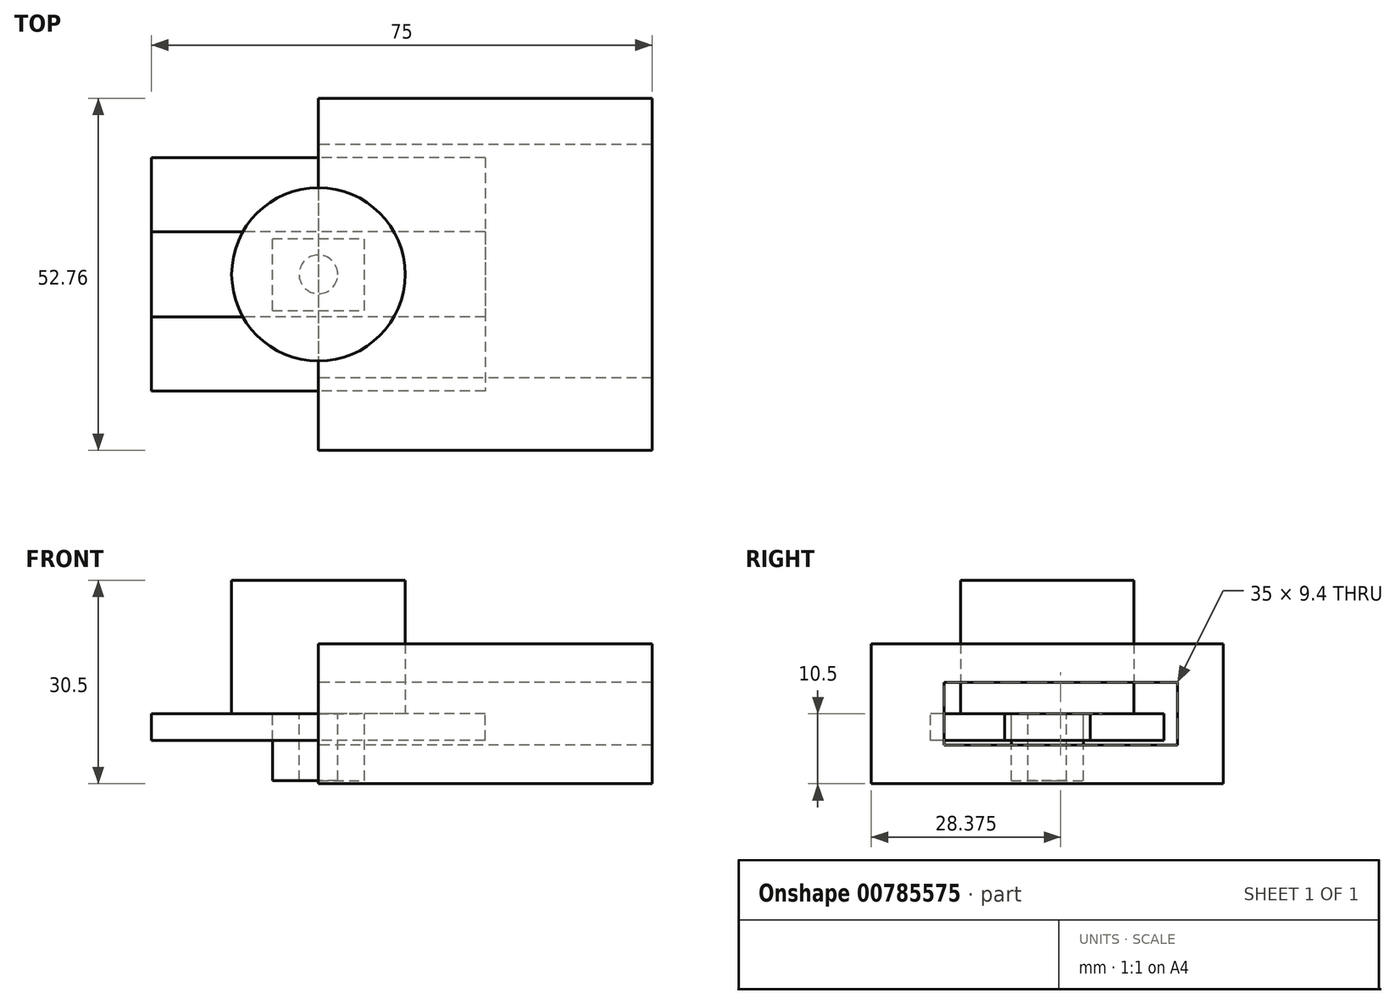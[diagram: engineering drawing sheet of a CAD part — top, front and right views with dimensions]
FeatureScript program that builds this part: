
annotation { "Feature Type Name" : "Feature", "Feature Type Description" : "" }
export const myFeature = defineFeature(function(context is Context, id is Id, definition is map)
    precondition{}
    {
        {
            var Q0;
            Q0=qCreatedBy(makeId("Top.planeOp"),FACE);
            var sketch = newSketch(context, id + "F0", { "sketchPlane" : qUnion([Q0])});
            skCircle(sketch, "E0", {"center": v(0, 0) * mm, "radius": 13 * mm});
            skSolve(sketch);
        }
        {
            var Q0;
            Q0 = qSketchRegion(id + "F0", true);
            extrude(context, id + "F1", {"entities" : qUnion([Q0]), "depth" : 20 * mm, "offsetDistance" : 25 * mm});
        }
        {
            var Q0;
            Q0=qCreatedBy(makeId("Top.planeOp"),FACE);
            var sketch = newSketch(context, id + "F2", { "sketchPlane" : qUnion([Q0])});
            skLineSegment(sketch, "E1.bottom", {"start": v(-6.9, -5.4) * mm, "end": v(6.9, -5.4) * mm});
            skLineSegment(sketch, "E1.top", {"start": v(-6.9, 5.4) * mm, "end": v(6.9, 5.4) * mm});
            skLineSegment(sketch, "E1.left", {"start": v(-6.9, -5.4) * mm, "end": v(-6.9, 5.4) * mm});
            skLineSegment(sketch, "E1.right", {"start": v(6.9, -5.4) * mm, "end": v(6.9, 5.4) * mm});
            skPoint(sketch, "E1.middle", {"position": v(0, 0) * mm});
            skSolve(sketch);
        }
        {
            var Q0;
            Q0 = qSketchRegion(id + "F2", true);
            extrude(context, id + "F3", {"entities" : qUnion([Q0]), "oppositeDirection" : true, "depth" : 10 * mm, "offsetDistance" : 25 * mm});
        }
        {
            var Q0;
            Q0=qCreatedBy(makeId("Top.planeOp"),FACE);
            var sketch = newSketch(context, id + "F4", { "sketchPlane" : qUnion([Q0])});
            skCircle(sketch, "E2", {"center": v(0, 0) * mm, "radius": 2.9 * mm});
            skSolve(sketch);
        }
        {
            var Q0;
            Q0 = qSketchRegion(id + "F4", true);
            extrude(context, id + "F5", {"entities" : qUnion([Q0]), "oppositeDirection" : true, "depth" : 10 * mm, "offsetDistance" : 25 * mm});
        }
        {
            var Q0;
            Q0=qCreatedBy(makeId("Top.planeOp"),FACE);
            var sketch = newSketch(context, id + "F6", { "sketchPlane" : qUnion([Q0])});
            skLineSegment(sketch, "E3.bottom", {"start": v(25, 6.4) * mm, "end": v(-25, 6.4) * mm});
            skLineSegment(sketch, "E3.top", {"start": v(25, -6.4) * mm, "end": v(-25, -6.4) * mm});
            skLineSegment(sketch, "E3.left", {"start": v(25, 6.4) * mm, "end": v(25, -6.4) * mm});
            skLineSegment(sketch, "E3.right", {"start": v(-25, 6.4) * mm, "end": v(-25, -6.4) * mm});
            skPoint(sketch, "E3.middle", {"position": v(0, 0) * mm});
            skSolve(sketch);
        }
        {
            var Q0;
            Q0 = qSketchRegion(id + "F6", true);
            extrude(context, id + "F7", {"entities" : qUnion([Q0]), "oppositeDirection" : true, "depth" : 4 * mm, "offsetDistance" : 25 * mm});
        }
        {
            var Q0;
            Q0=qCreatedBy(makeId("Top.planeOp"),FACE);
            var sketch = newSketch(context, id + "F8", { "sketchPlane" : qUnion([Q0])});
            skLineSegment(sketch, "E4.bottom", {"start": v(25, 17.5) * mm, "end": v(-25, 17.5) * mm});
            skLineSegment(sketch, "E4.top", {"start": v(25, -17.5) * mm, "end": v(-25, -17.5) * mm});
            skLineSegment(sketch, "E4.left", {"start": v(25, 17.5) * mm, "end": v(25, -17.5) * mm});
            skLineSegment(sketch, "E4.right", {"start": v(-25, 17.5) * mm, "end": v(-25, -17.5) * mm});
            skPoint(sketch, "E4.middle", {"position": v(0, 0) * mm});
            skSolve(sketch);
        }
        {
            var Q0;
            Q0 = qSketchRegion(id + "F8", true);
            extrude(context, id + "F9", {"entities" : qUnion([Q0]), "oppositeDirection" : true, "depth" : 4 * mm, "offsetDistance" : 25 * mm});
        }
        {
            var Q0;
            Q0=qCreatedBy(makeId("Right.planeOp"),FACE);
            var sketch = newSketch(context, id + "F10", { "sketchPlane" : qUnion([Q0])});
            skLineSegment(sketch, "E5.bottom", {"start": v(19.5, 4.7) * mm, "end": v(-15.5, 4.7) * mm});
            skLineSegment(sketch, "E5.top", {"start": v(19.5, -4.7) * mm, "end": v(-15.5, -4.7) * mm});
            skLineSegment(sketch, "E5.left", {"start": v(19.5, 4.7) * mm, "end": v(19.5, -4.7) * mm});
            skLineSegment(sketch, "E5.right", {"start": v(-15.5, 4.7) * mm, "end": v(-15.5, -4.7) * mm});
            skPoint(sketch, "E5.middle", {"position": v(2, 0) * mm});
            skLineSegment(sketch, "E6.bottom", {"start": v(26.38, 10.5) * mm, "end": v(-26.38, 10.5) * mm});
            skLineSegment(sketch, "E6.top", {"start": v(26.38, -10.5) * mm, "end": v(-26.38, -10.5) * mm});
            skLineSegment(sketch, "E6.left", {"start": v(26.38, 10.5) * mm, "end": v(26.38, -10.5) * mm});
            skLineSegment(sketch, "E6.right", {"start": v(-26.38, 10.5) * mm, "end": v(-26.38, -10.5) * mm});
            skPoint(sketch, "E6.middle", {"position": v(0, 0) * mm});
            skSolve(sketch);
        }
        {
            var Q0;
            Q0 = qSketchRegion(id + "F10", true);
            extrude(context, id + "F11", {"entities" : qUnion([Q0]), "depth" : 50 * mm, "offsetDistance" : 25 * mm});
        }
    });
